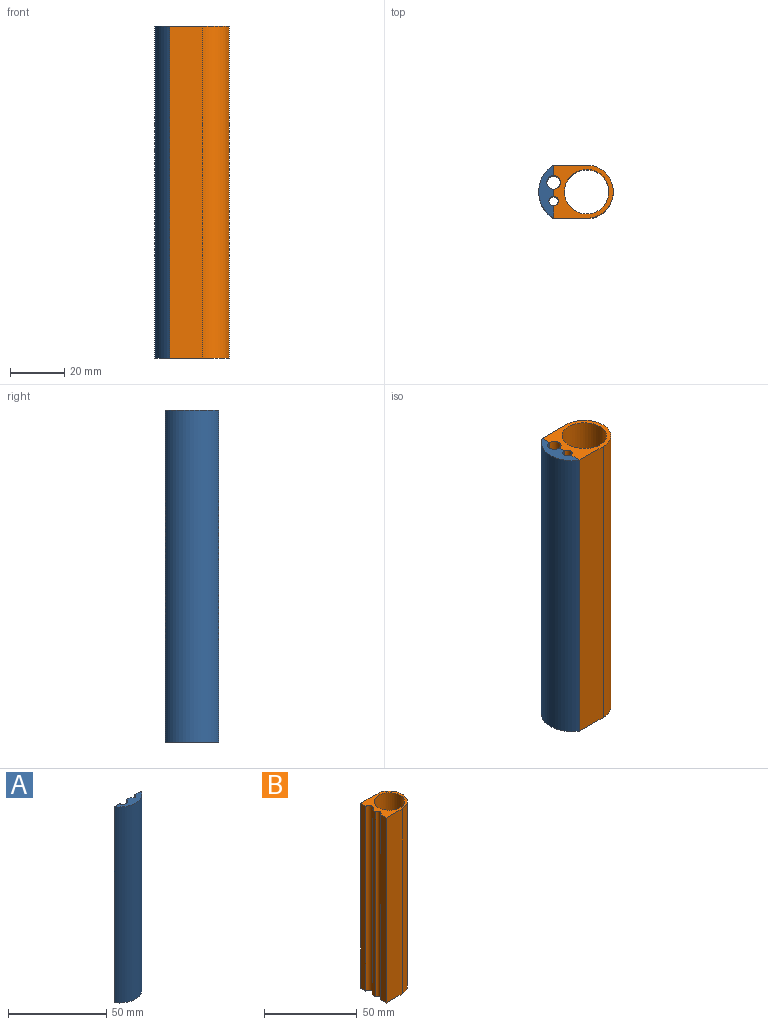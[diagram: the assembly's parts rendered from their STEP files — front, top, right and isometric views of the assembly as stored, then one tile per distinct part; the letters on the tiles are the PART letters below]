
ASSEMBLY  parts=2 mates=1
PART A: 8 faces, bbox 19.6x5.5x122.2 mm
  f0: plane 122.17x2.64mm, normal (0,1,0), area 322.7mm2, adj f1,f5,f6,f7
  f1: cylinder r=2.48mm len=122.17mm, axis (0,0,-1), area 950.5mm2, adj f0,f2,f6,f7
  f2: plane 122.17x3.89mm, normal (0,1,0), area 474.8mm2, adj f1,f3,f6,f7
  f3: cylinder r=11.46mm len=122.17mm, axis (0,0,-1), area 2863.3mm2, adj f2,f4,f6,f7
  f4: plane 122.17x4.65mm, normal (0,1,0), area 567.9mm2, adj f3,f5,f6,f7
  f5: cylinder r=1.71mm len=122.17mm, axis (0,0,-1), area 658.1mm2, adj f0,f4,f6,f7
  f6: plane 19.56x5.49mm, normal (0,0,1), area 61.6mm2, adj f0,f1,f2,f3,f4,f5
  f7: plane 19.56x5.49mm, normal (0,0,-1), area 61.6mm2, adj f0,f1,f2,f3,f4,f5
PART B: 11 faces, bbox 22x19.6x122.2 mm
  f0: cylinder r=1.71mm len=122.17mm, axis (0,0,-1), area 658.1mm2, adj f1,f7,f9,f10
  f1: plane 122.17x4.65mm, normal (-1,0,0), area 567.9mm2, adj f0,f2,f9,f10
  f2: plane 122.17x12.19mm, normal (0,-1,0), area 1489.5mm2, adj f1,f3,f9,f10
  f3: cylinder r=9.78mm len=122.17mm, axis (0,0,-1), area 3753.4mm2, adj f2,f4,f9,f10
  f4: plane 122.17x12.19mm, normal (0,1,0), area 1489.5mm2, adj f3,f5,f9,f10
  f5: plane 122.17x3.89mm, normal (-1,0,0), area 474.8mm2, adj f4,f6,f9,f10
  f6: cylinder r=2.48mm len=122.17mm, axis (0,0,-1), area 950.5mm2, adj f5,f7,f9,f10
  f7: plane 122.17x2.64mm, normal (-1,0,0), area 322.7mm2, adj f0,f6,f9,f10
  f8: cylinder r=8.19mm len=122.17mm, axis (0,0,-1), area 6288.1mm2, adj f9,f10
  f9: plane 21.97x19.56mm, normal (0,0,1), area 163.6mm2, adj f0,f1,f2,f3,f4,f5,f6,f7
  f10: plane 21.97x19.56mm, normal (0,0,-1), area 163.6mm2, adj f0,f1,f2,f3,f4,f5,f6,f7
PLACE A rot(axis=(0,0,-1),90deg) t=(-18.33,25.97,45.32)mm
PLACE B t=(-6.14,25.97,-15.77)mm
MATE fastened A.f4 <-> B.f1  axis (1,0,0) through (-18.33,16.19,106.4)mm
